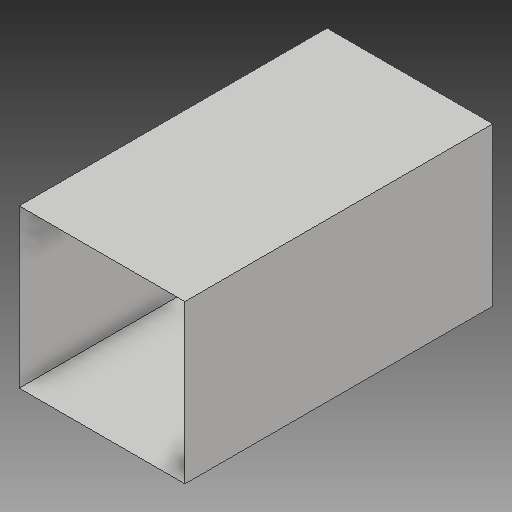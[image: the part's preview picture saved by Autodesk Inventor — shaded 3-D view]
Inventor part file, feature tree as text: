
AUTODESK INVENTOR PART (.ipt)
format: ipt  version: 2017 (Build 210142000, 142)  size: 89,600 bytes
history: native  units: in
note: dims shown in document units (in); Inventor stores cm internally (conversion verified against a paired STEP export)
features: extrude x1, other x1, sketch x1
ambient origin geometry x8: Origin, YZ Plane, XZ Plane, XY Plane, X Axis, Y Axis, Z Axis, Center Point
bodies: Solid1 (feature_tree)
feature tree (3):
  extrude  "corridor"  Depth=7.0in
  other  "removed ends"
  sketch  "Sketch1"  dims[d0=6.6667in d1=7.0in d2=13.0in d3=0.0in]
